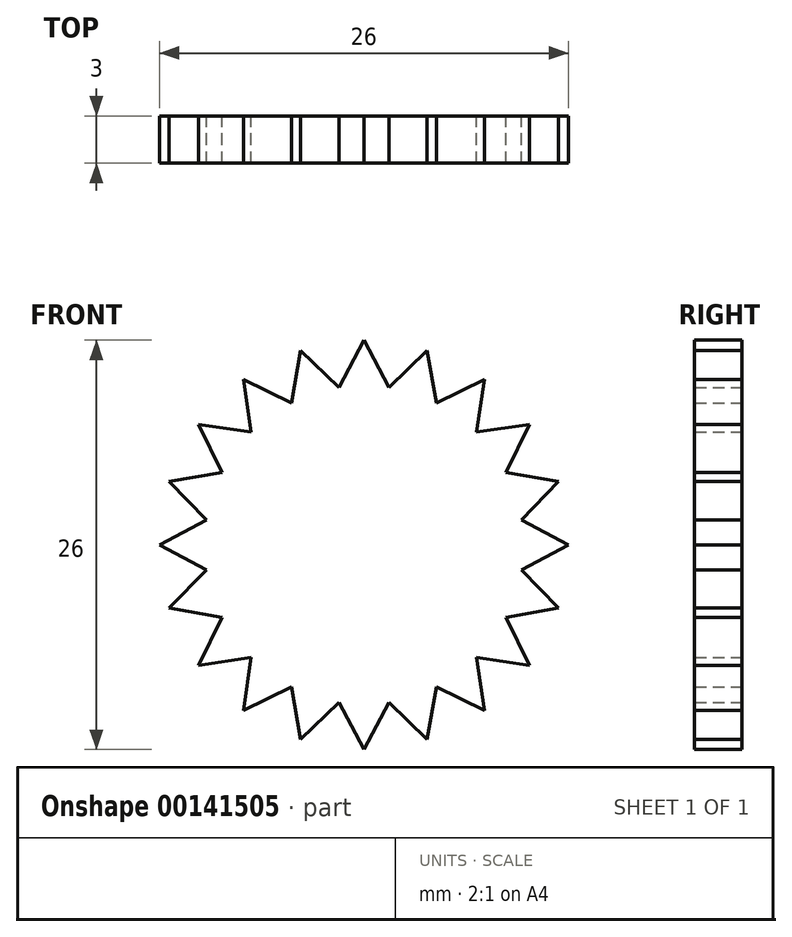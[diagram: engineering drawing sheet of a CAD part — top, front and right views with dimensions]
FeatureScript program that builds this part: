
annotation { "Feature Type Name" : "Feature", "Feature Type Description" : "" }
export const myFeature = defineFeature(function(context is Context, id is Id, definition is map)
    precondition{}
    {
        {
            var Q0;
            Q0=qCreatedBy(makeId("Front.planeOp"),FACE);
            var sketch = newSketch(context, id + "F0", { "sketchPlane" : qUnion([Q0])});
            skLineSegment(sketch, "E0.0", {"start": v(10, 1.58) * mm, "end": v(10, -1.58) * mm});
            skLineSegment(sketch, "E0.1", {"start": v(10, -1.58) * mm, "end": v(9.02, -4.6) * mm});
            skLineSegment(sketch, "E0.2", {"start": v(9.02, -4.6) * mm, "end": v(7.16, -7.16) * mm});
            skLineSegment(sketch, "E0.3", {"start": v(7.16, -7.16) * mm, "end": v(4.6, -9.02) * mm});
            skLineSegment(sketch, "E0.4", {"start": v(4.6, -9.02) * mm, "end": v(1.58, -10) * mm});
            skLineSegment(sketch, "E0.5", {"start": v(1.58, -10) * mm, "end": v(-1.58, -10) * mm});
            skLineSegment(sketch, "E0.6", {"start": v(-1.58, -10) * mm, "end": v(-4.6, -9.02) * mm});
            skLineSegment(sketch, "E0.7", {"start": v(-4.6, -9.02) * mm, "end": v(-7.16, -7.16) * mm});
            skLineSegment(sketch, "E0.8", {"start": v(-7.16, -7.16) * mm, "end": v(-9.02, -4.6) * mm});
            skLineSegment(sketch, "E0.9", {"start": v(-9.02, -4.6) * mm, "end": v(-10, -1.58) * mm});
            skLineSegment(sketch, "E0.10", {"start": v(-10, -1.58) * mm, "end": v(-10, 1.58) * mm});
            skLineSegment(sketch, "E0.11", {"start": v(-10, 1.58) * mm, "end": v(-9.02, 4.6) * mm});
            skLineSegment(sketch, "E0.12", {"start": v(-9.02, 4.6) * mm, "end": v(-7.16, 7.16) * mm});
            skLineSegment(sketch, "E0.13", {"start": v(-7.16, 7.16) * mm, "end": v(-4.6, 9.02) * mm});
            skLineSegment(sketch, "E0.14", {"start": v(-4.6, 9.02) * mm, "end": v(-1.58, 10) * mm});
            skLineSegment(sketch, "E0.15", {"start": v(-1.58, 10) * mm, "end": v(1.58, 10) * mm});
            skLineSegment(sketch, "E0.16", {"start": v(1.58, 10) * mm, "end": v(4.6, 9.02) * mm});
            skLineSegment(sketch, "E0.17", {"start": v(4.6, 9.02) * mm, "end": v(7.16, 7.16) * mm});
            skLineSegment(sketch, "E0.18", {"start": v(7.16, 7.16) * mm, "end": v(9.02, 4.6) * mm});
            skLineSegment(sketch, "E0.19", {"start": v(9.02, 4.6) * mm, "end": v(10, 1.58) * mm});
            skPoint(sketch, "E0.0.midPoint", {"position": v(10, 0) * mm});
            skLineSegment(sketch, "E1", {"start": v(-1.58, 10) * mm, "end": v(0, 13) * mm});
            skLineSegment(sketch, "E2", {"start": v(1.58, 10) * mm, "end": v(0, 13) * mm});
            skLineSegment(sketch, "E3.1.0", {"start": v(-1.58, 10) * mm, "end": v(-4.02, 12.36) * mm});
            skLineSegment(sketch, "E3.1.1", {"start": v(-4.6, 9.02) * mm, "end": v(-4.02, 12.36) * mm});
            skLineSegment(sketch, "E3.2.0", {"start": v(-4.6, 9.02) * mm, "end": v(-7.64, 10.52) * mm});
            skLineSegment(sketch, "E3.2.1", {"start": v(-7.16, 7.16) * mm, "end": v(-7.64, 10.52) * mm});
            skLineSegment(sketch, "E3.3.0", {"start": v(-7.16, 7.16) * mm, "end": v(-10.52, 7.64) * mm});
            skLineSegment(sketch, "E3.3.1", {"start": v(-9.02, 4.6) * mm, "end": v(-10.52, 7.64) * mm});
            skLineSegment(sketch, "E3.4.0", {"start": v(-9.02, 4.6) * mm, "end": v(-12.36, 4.02) * mm});
            skLineSegment(sketch, "E3.4.1", {"start": v(-10, 1.58) * mm, "end": v(-12.36, 4.02) * mm});
            skLineSegment(sketch, "E3.5.0", {"start": v(-10, 1.58) * mm, "end": v(-13, 0) * mm});
            skLineSegment(sketch, "E3.5.1", {"start": v(-10, -1.58) * mm, "end": v(-13, 0) * mm});
            skLineSegment(sketch, "E3.6.0", {"start": v(-10, -1.58) * mm, "end": v(-12.36, -4.02) * mm});
            skLineSegment(sketch, "E3.6.1", {"start": v(-9.02, -4.6) * mm, "end": v(-12.36, -4.02) * mm});
            skLineSegment(sketch, "E3.7.0", {"start": v(-9.02, -4.6) * mm, "end": v(-10.52, -7.64) * mm});
            skLineSegment(sketch, "E3.7.1", {"start": v(-7.16, -7.16) * mm, "end": v(-10.52, -7.64) * mm});
            skLineSegment(sketch, "E3.8.0", {"start": v(-7.16, -7.16) * mm, "end": v(-7.64, -10.52) * mm});
            skLineSegment(sketch, "E3.8.1", {"start": v(-4.6, -9.02) * mm, "end": v(-7.64, -10.52) * mm});
            skLineSegment(sketch, "E3.9.0", {"start": v(-4.6, -9.02) * mm, "end": v(-4.02, -12.36) * mm});
            skLineSegment(sketch, "E3.9.1", {"start": v(-1.58, -10) * mm, "end": v(-4.02, -12.36) * mm});
            skLineSegment(sketch, "E3.10.0", {"start": v(-1.58, -10) * mm, "end": v(0, -13) * mm});
            skLineSegment(sketch, "E3.10.1", {"start": v(1.58, -10) * mm, "end": v(0, -13) * mm});
            skLineSegment(sketch, "E3.11.0", {"start": v(1.58, -10) * mm, "end": v(4.02, -12.36) * mm});
            skLineSegment(sketch, "E3.11.1", {"start": v(4.6, -9.02) * mm, "end": v(4.02, -12.36) * mm});
            skLineSegment(sketch, "E3.12.0", {"start": v(4.6, -9.02) * mm, "end": v(7.64, -10.52) * mm});
            skLineSegment(sketch, "E3.12.1", {"start": v(7.16, -7.16) * mm, "end": v(7.64, -10.52) * mm});
            skLineSegment(sketch, "E3.13.0", {"start": v(7.16, -7.16) * mm, "end": v(10.52, -7.64) * mm});
            skLineSegment(sketch, "E3.13.1", {"start": v(9.02, -4.6) * mm, "end": v(10.52, -7.64) * mm});
            skLineSegment(sketch, "E3.14.0", {"start": v(9.02, -4.6) * mm, "end": v(12.36, -4.02) * mm});
            skLineSegment(sketch, "E3.14.1", {"start": v(10, -1.58) * mm, "end": v(12.36, -4.02) * mm});
            skLineSegment(sketch, "E3.15.0", {"start": v(10, -1.58) * mm, "end": v(13, 0) * mm});
            skLineSegment(sketch, "E3.15.1", {"start": v(10, 1.58) * mm, "end": v(13, 0) * mm});
            skLineSegment(sketch, "E3.16.0", {"start": v(10, 1.58) * mm, "end": v(12.36, 4.02) * mm});
            skLineSegment(sketch, "E3.16.1", {"start": v(9.02, 4.6) * mm, "end": v(12.36, 4.02) * mm});
            skLineSegment(sketch, "E3.17.0", {"start": v(9.02, 4.6) * mm, "end": v(10.52, 7.64) * mm});
            skLineSegment(sketch, "E3.17.1", {"start": v(7.16, 7.16) * mm, "end": v(10.52, 7.64) * mm});
            skLineSegment(sketch, "E3.18.0", {"start": v(7.16, 7.16) * mm, "end": v(7.64, 10.52) * mm});
            skLineSegment(sketch, "E3.18.1", {"start": v(4.6, 9.02) * mm, "end": v(7.64, 10.52) * mm});
            skLineSegment(sketch, "E3.19.0", {"start": v(4.6, 9.02) * mm, "end": v(4.02, 12.36) * mm});
            skLineSegment(sketch, "E3.19.1", {"start": v(1.58, 10) * mm, "end": v(4.02, 12.36) * mm});
            skPoint(sketch, "E3.center", {"position": v(0, 0) * mm});
            skSolve(sketch);
        }
        {
            var Q0;
            Q0 = qSketchRegion(id + "F0", true);
            extrude(context, id + "F1", {"entities" : qUnion([Q0]), "depth" : 3 * mm});
        }
    });
